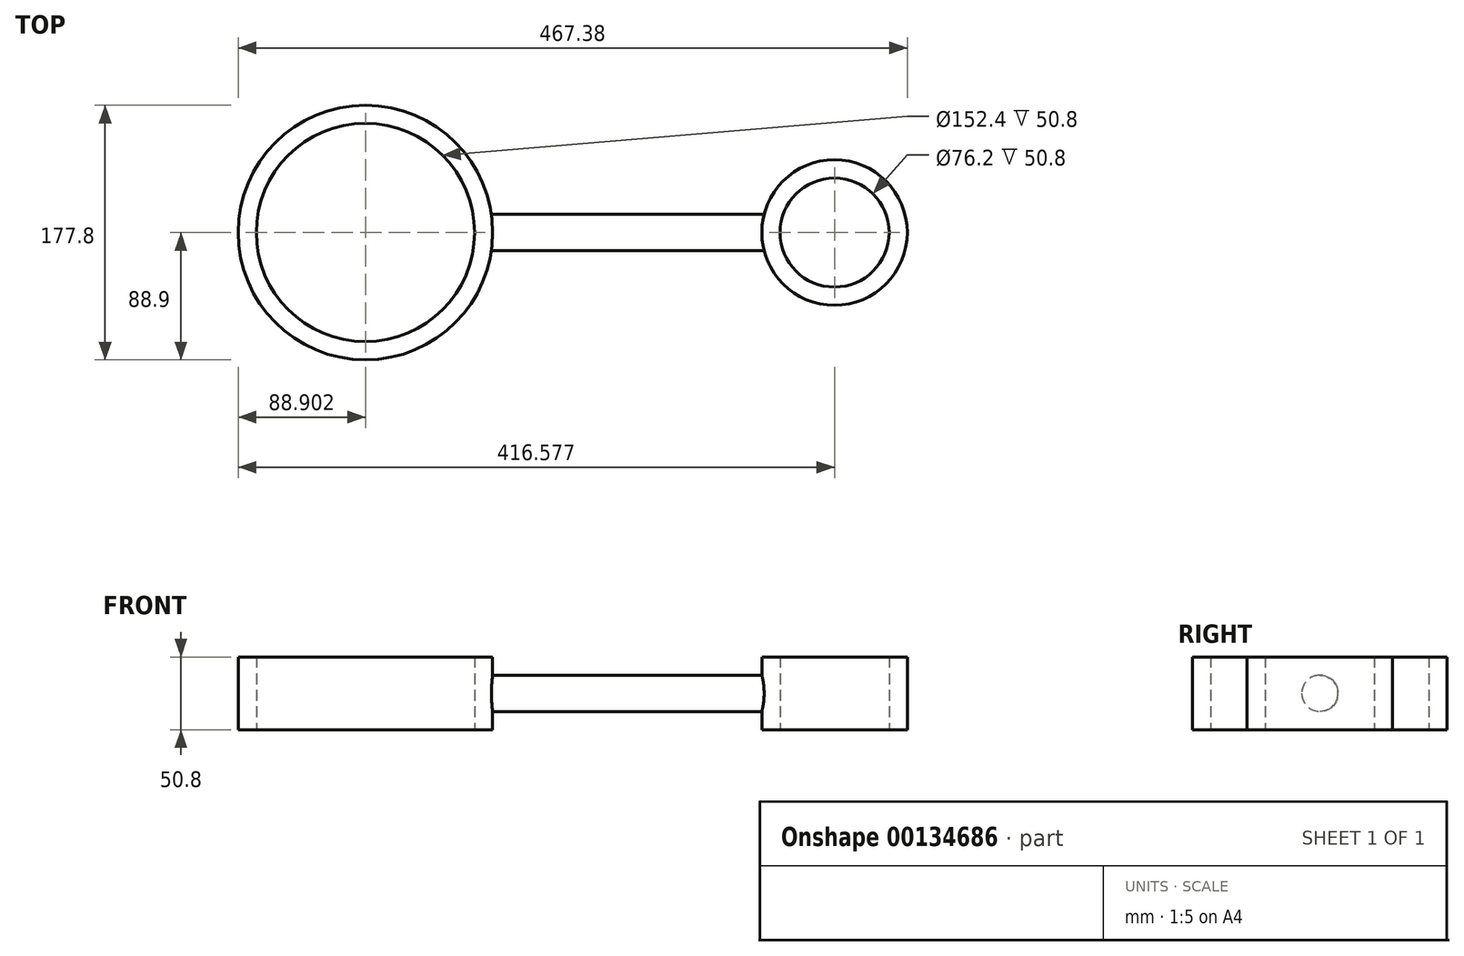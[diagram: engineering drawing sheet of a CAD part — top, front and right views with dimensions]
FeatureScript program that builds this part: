
annotation { "Feature Type Name" : "Feature", "Feature Type Description" : "" }
export const myFeature = defineFeature(function(context is Context, id is Id, definition is map)
    precondition{}
    {
        {
            var Q0;
            Q0=qCreatedBy(makeId("Right.planeOp"),FACE);
            var sketch = newSketch(context, id + "F0", { "sketchPlane" : qUnion([Q0])});
            skCircle(sketch, "E0", {"center": v(0, 0) * mm, "radius": 12.7 * mm});
            skSolve(sketch);
        }
        {
            var Q0;
            Q0=makeQuery(id+"F0.imprint","IMPRINT",FACE,{"disambiguationData":[TD([[makeQuery(id+"F0.imprint","IMPRINT",EDGE,{"derivedFrom":sQuery(id+"F0.wireOp",EDGE,"E0")}),1.0]])]});
            extrude(context, id + "F1", {"entities" : qUnion([Q0]), "endBound" : BoundingType.SYMMETRIC, "depth" : 190.5 * mm});
        }
        {
            var Q0;
            Q0=qCreatedBy(makeId("Top.planeOp"),FACE);
            var sketch = newSketch(context, id + "F2", { "sketchPlane" : qUnion([Q0])});
            skLineSegment(sketch, "E1.0", {"start": v(95.25, 12.7) * mm, "end": v(95.25, -12.7) * mm});
            skLineSegment(sketch, "E2.0", {"start": v(-95.25, 12.7) * mm, "end": v(-95.25, -12.7) * mm});
            skCircle(sketch, "E3", {"center": v(-183.24, 0) * mm, "radius": 88.9 * mm});
            skPoint(sketch, "E3.first.point", {"position": v(-272.14, 0) * mm});
            skCircle(sketch, "E4", {"center": v(-183.24, 0) * mm, "radius": 76.2 * mm});
            skSolve(sketch);
        }
        {
            var Q0;
            Q0 = qSketchRegion(id + "F2", true);
            extrude(context, id + "F3", {"entities" : qUnion([Q0]), "operationType" : NewBodyOperationType.ADD, "endBound" : BoundingType.SYMMETRIC, "depth" : 50.8 * mm});
        }
        {
            var Q0;
            Q0=qCreatedBy(makeId("Top.planeOp"),FACE);
            var sketch = newSketch(context, id + "F4", { "sketchPlane" : qUnion([Q0])});
            skLineSegment(sketch, "E5.0", {"start": v(95.25, 12.7) * mm, "end": v(95.25, -12.7) * mm});
            skCircle(sketch, "E6", {"center": v(144.44, 0) * mm, "radius": 50.8 * mm});
            skPoint(sketch, "E6.first.point", {"position": v(195.24, 0) * mm});
            skCircle(sketch, "E7", {"center": v(144.44, 0) * mm, "radius": 38.1 * mm});
            skSolve(sketch);
        }
        {
            var Q0;
            {var subQ0=sQuery(id+"F4.wireOp",EDGE,"E5.0");Q0=makeQuery(id+"F4.imprint","IMPRINT",FACE,{"disambiguationData":[TD([[makeQuery(id+"F4.imprint","IMPRINT",EDGE,{"derivedFrom":subQ0}),-1.0]])]});}
            var Q1;
            {var subQ0=sQuery(id+"F4.wireOp",EDGE,"E5.0");Q1=makeQuery(id+"F4.imprint","IMPRINT",FACE,{"disambiguationData":[TD([[makeQuery(id+"F4.imprint","IMPRINT",EDGE,{"derivedFrom":subQ0}),1.0]])]});}
            extrude(context, id + "F5", {"entities" : qUnion([Q0, Q1]), "operationType" : NewBodyOperationType.ADD, "endBound" : BoundingType.SYMMETRIC, "depth" : 50.8 * mm});
        }
    });
